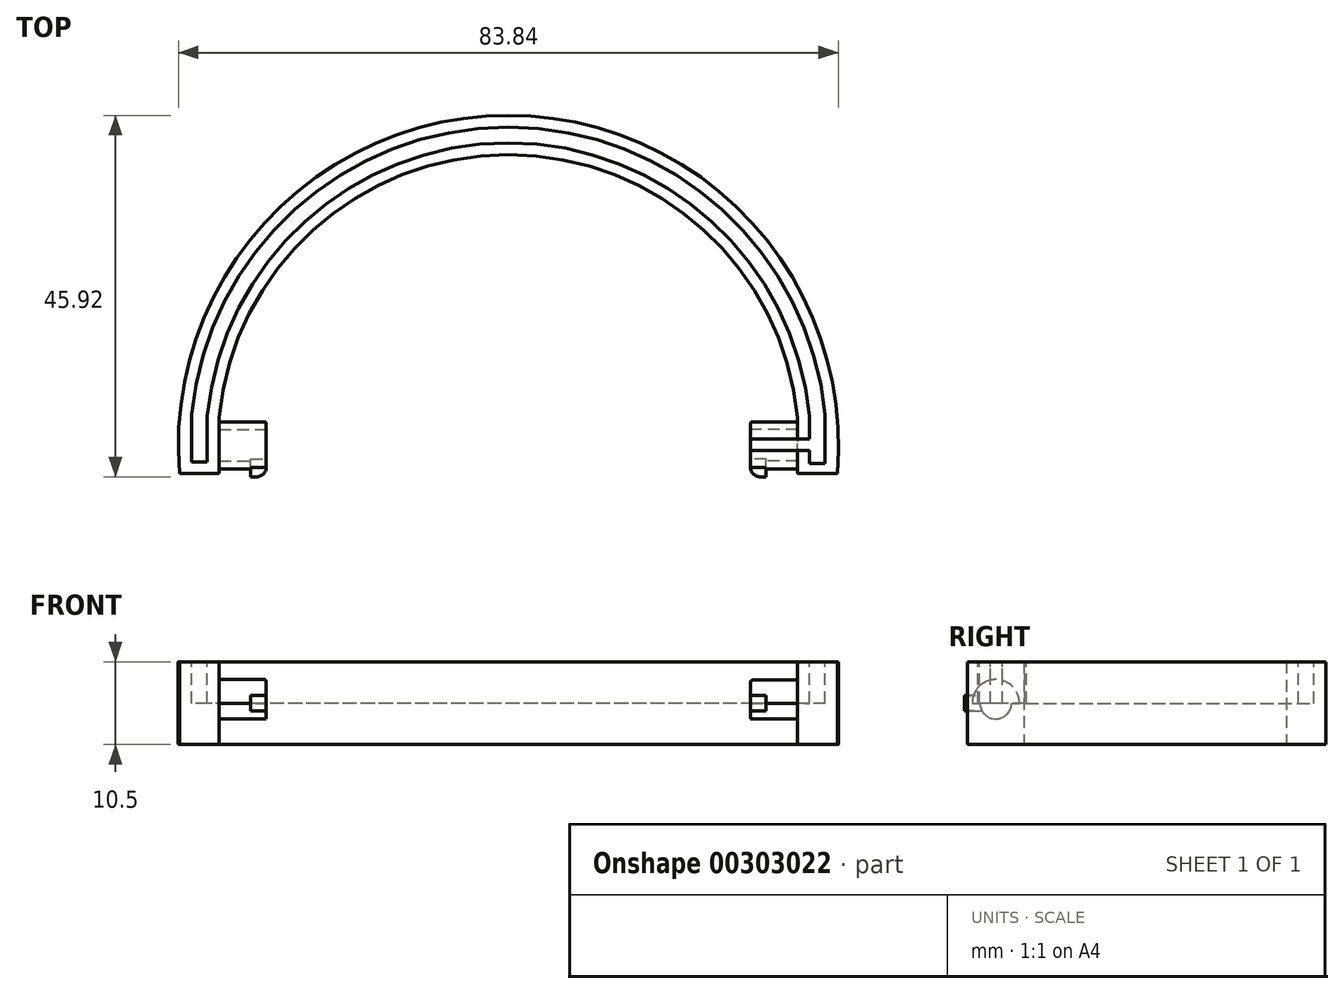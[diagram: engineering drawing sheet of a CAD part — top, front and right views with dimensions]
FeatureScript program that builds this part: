
annotation { "Feature Type Name" : "Feature", "Feature Type Description" : "" }
export const myFeature = defineFeature(function(context is Context, id is Id, definition is map)
    precondition{}
    {
        {
            var Q0;
            Q0=qCreatedBy(makeId("Top.planeOp"),FACE);
            var sketch = newSketch(context, id + "F0", { "sketchPlane" : qUnion([Q0])});
            skArc(sketch, "E0", {"start": v(36.75, 7.15) * mm, "mid": v(0, 40.5) * mm, "end": v(-36.75, 7.15) * mm});
            skPoint(sketch, "E1.center.orphan", {"position": v(0, 0) * mm});
            skArc(sketch, "E2.0", {"start": v(41.77, 0) * mm, "mid": v(0, 45.5) * mm, "end": v(-41.77, 0) * mm});
            skLineSegment(sketch, "E3", {"start": v(-36.75, 0) * mm, "end": v(-36.75, 7.15) * mm});
            skLineSegment(sketch, "E4", {"start": v(-36.75, 0) * mm, "end": v(-41.77, 0) * mm});
            skLineSegment(sketch, "E5", {"start": v(36.75, 0) * mm, "end": v(36.75, 7.15) * mm});
            skLineSegment(sketch, "E6", {"start": v(36.75, 0) * mm, "end": v(41.77, 0) * mm});
            skSolve(sketch);
        }
        {
            var Q0;
            Q0 = qSketchRegion(id + "F0", true);
            extrude(context, id + "F1", {"entities" : qUnion([Q0]), "depth" : 10.5 * mm});
        }
        {
            var Q0;
            Q0=makeQuery(id+"F1.opExtrude","SWEPT_FACE",FACE,{"disambiguationData":[OSD([sQuery(id+"F0.wireOp",EDGE,"E3")])]});
            var sketch = newSketch(context, id + "F2", { "sketchPlane" : qUnion([Q0])});
            skCircle(sketch, "E7", {"center": v(3.58, 5.25) * mm, "radius": 3 * mm});
            skPoint(sketch, "E7.centerSnap0", {"position": v(3.58, 0) * mm});
            skPoint(sketch, "E7.centerSnap1", {"position": v(0, 5.25) * mm});
            skSolve(sketch);
        }
        {
            var Q0;
            Q0=makeQuery(id+"F2.imprint","IMPRINT",FACE,{"disambiguationData":[TD([[makeQuery(id+"F2.imprint","IMPRINT",EDGE,{"derivedFrom":sQuery(id+"F2.wireOp",EDGE,"E7")}),1.0]])]});
            extrude(context, id + "F3", {"entities" : qUnion([Q0]), "operationType" : NewBodyOperationType.ADD, "depth" : 6 * mm});
        }
        {
            var Q0;
            Q0=makeQuery(id+"F1.opExtrude","SWEPT_FACE",FACE,{"disambiguationData":[OSD([sQuery(id+"F0.wireOp",EDGE,"E5")])]});
            var sketch = newSketch(context, id + "F4", { "sketchPlane" : qUnion([Q0])});
            skCircle(sketch, "E8", {"center": v(-3.58, 5.25) * mm, "radius": 3 * mm});
            skPoint(sketch, "E8.centerSnap0", {"position": v(-3.58, 10.5) * mm});
            skPoint(sketch, "E8.centerSnap1", {"position": v(0, 5.25) * mm});
            skSolve(sketch);
        }
        {
            var Q0;
            Q0 = qSketchRegion(id + "F4", true);
            extrude(context, id + "F5", {"entities" : qUnion([Q0]), "operationType" : NewBodyOperationType.ADD, "depth" : 6 * mm});
        }
        {
            var Q0;
            Q0=makeQuery(id+"F1.opExtrude","CAP_FACE",FACE,{"disambiguationData":[OSD([sQuery(id+"F0.wireOp",EDGE,"E0"),sQuery(id+"F0.wireOp",EDGE,"E2.0"),sQuery(id+"F0.wireOp",EDGE,"E3"),sQuery(id+"F0.wireOp",EDGE,"E4"),sQuery(id+"F0.wireOp",EDGE,"E5"),sQuery(id+"F0.wireOp",EDGE,"E6")])],"isStart":false});
            var sketch = newSketch(context, id + "F6", { "sketchPlane" : qUnion([Q0])});
            skArc(sketch, "E9.0", {"start": v(38.24, 7.3) * mm, "mid": v(0, 42) * mm, "end": v(-38.24, 7.3) * mm});
            skArc(sketch, "E10.0", {"start": v(40.23, 7.5) * mm, "mid": v(0, 44) * mm, "end": v(-40.23, 7.5) * mm});
            skLineSegment(sketch, "E11", {"start": v(-40.23, 7.5) * mm, "end": v(-40.23, 1.5) * mm});
            skLineSegment(sketch, "E12", {"start": v(-38.24, 7.3) * mm, "end": v(-38.24, 1.5) * mm});
            skLineSegment(sketch, "E13", {"start": v(-38.24, 1.5) * mm, "end": v(-40.23, 1.5) * mm});
            skLineSegment(sketch, "E14", {"start": v(38.24, 7.3) * mm, "end": v(38.24, 4.4) * mm});
            skLineSegment(sketch, "E15", {"start": v(40.23, 7.5) * mm, "end": v(40.23, 1.3) * mm});
            skLineSegment(sketch, "E16", {"start": v(40.23, 1.3) * mm, "end": v(38.24, 1.3) * mm});
            skLineSegment(sketch, "E17", {"start": v(30.74, 4.4) * mm, "end": v(38.24, 4.4) * mm});
            skLineSegment(sketch, "E18", {"start": v(30.74, 2.9) * mm, "end": v(38.24, 2.9) * mm});
            skPoint(sketch, "E19", {"position": v(38.24, 3.65) * mm});
            skLineSegment(sketch, "E20", {"start": v(30.74, 4.4) * mm, "end": v(30.74, 2.9) * mm});
            skLineSegment(sketch, "E21.trimOffspring", {"start": v(38.24, 2.9) * mm, "end": v(38.24, 1.3) * mm});
            skSolve(sketch);
        }
        {
            var Q0;
            Q0 = qSketchRegion(id + "F6", true);
            extrude(context, id + "F7", {"entities" : qUnion([Q0]), "operationType" : NewBodyOperationType.REMOVE, "oppositeDirection" : true, "depth" : 5.25 * mm});
        }
        {
            var Q0;
            Q0=makeQuery(id+"F5.opExtrude","CAP_FACE",FACE,{"disambiguationData":[OSD([sQuery(id+"F4.wireOp",EDGE,"E8")])],"isStart":false});
            var sketch = newSketch(context, id + "F8", { "sketchPlane" : qUnion([Q0])});
            skArc(sketch, "E22", {"start": v(-5.58, 5.25) * mm, "mid": v(-3.58, 3.25) * mm, "end": v(-1.58, 5.25) * mm});
            skLineSegment(sketch, "E23", {"start": v(-5.58, 5.25) * mm, "end": v(-6.58, 5.25) * mm});
            skLineSegment(sketch, "E24", {"start": v(-6.58, 5.25) * mm, "end": v(-5.58, 5.25) * mm});
            skLineSegment(sketch, "E25.trimOffspring", {"start": v(-1.58, 5.25) * mm, "end": v(-0.58, 5.25) * mm});
            skArc(sketch, "E26", {"start": v(-6.58, 5.25) * mm, "mid": v(-3.58, 2.25) * mm, "end": v(-0.58, 5.25) * mm});
            skSolve(sketch);
        }
        {
            var Q0;
            Q0=makeQuery(id+"F8.imprint","IMPRINT",FACE,{"disambiguationData":[TD([[makeQuery(id+"F8.imprint","IMPRINT",EDGE,{"derivedFrom":sQuery(id+"F8.wireOp",EDGE,"E22")}),-1.0]])]});
            extrude(context, id + "F9", {"entities" : qUnion([Q0]), "operationType" : NewBodyOperationType.REMOVE, "oppositeDirection" : true, "depth" : 6 * mm});
        }
        {
            var Q0;
            Q0=makeQuery(id+"F3.opExtrude","CAP_FACE",FACE,{"disambiguationData":[OSD([sQuery(id+"F2.wireOp",EDGE,"E7")])],"isStart":false});
            var sketch = newSketch(context, id + "F10", { "sketchPlane" : qUnion([Q0])});
            skArc(sketch, "E27", {"start": v(1.58, 5.25) * mm, "mid": v(3.58, 3.25) * mm, "end": v(5.58, 5.25) * mm});
            skLineSegment(sketch, "E28", {"start": v(5.58, 5.25) * mm, "end": v(6.58, 5.25) * mm});
            skLineSegment(sketch, "E29", {"start": v(6.58, 5.25) * mm, "end": v(5.58, 5.25) * mm});
            skLineSegment(sketch, "E30.trimOffspring", {"start": v(1.58, 5.25) * mm, "end": v(0.58, 5.25) * mm});
            skArc(sketch, "E31", {"start": v(0.58, 5.25) * mm, "mid": v(3.58, 2.25) * mm, "end": v(6.58, 5.25) * mm});
            skSolve(sketch);
        }
        {
            var Q0;
            Q0 = qSketchRegion(id + "F10", true);
            extrude(context, id + "F11", {"entities" : qUnion([Q0]), "operationType" : NewBodyOperationType.REMOVE, "oppositeDirection" : true, "depth" : 6 * mm});
        }
        {
            var Q0;
            Q0=makeQuery(id+"F5.opExtrude","CAP_FACE",FACE,{"disambiguationData":[OSD([sQuery(id+"F4.wireOp",EDGE,"E8")])],"isStart":false});
            var sketch = newSketch(context, id + "F12", { "sketchPlane" : qUnion([Q0])});
            skLineSegment(sketch, "E32.bottom", {"start": v(0.42, 6.25) * mm, "end": v(-1.58, 6.25) * mm});
            skLineSegment(sketch, "E32.top", {"start": v(0.42, 4.25) * mm, "end": v(-1.58, 4.25) * mm});
            skLineSegment(sketch, "E32.left", {"start": v(0.42, 6.25) * mm, "end": v(0.42, 4.25) * mm});
            skPoint(sketch, "E32.middle", {"position": v(-1.58, 5.25) * mm});
            skLineSegment(sketch, "E33", {"start": v(-1.58, 4.25) * mm, "end": v(-2.3, 4.25) * mm});
            skLineSegment(sketch, "E34", {"start": v(-2.3, 4.25) * mm, "end": v(-1.58, 6.25) * mm});
            skSolve(sketch);
        }
        {
            var Q0;
            Q0 = qSketchRegion(id + "F12", true);
            extrude(context, id + "F13", {"entities" : qUnion([Q0]), "operationType" : NewBodyOperationType.ADD, "oppositeDirection" : true, "depth" : 2 * mm});
        }
        {
            var Q0;
            Q0=makeQuery(id+"F3.opExtrude","CAP_FACE",FACE,{"disambiguationData":[OSD([sQuery(id+"F2.wireOp",EDGE,"E7")])],"isStart":false});
            var sketch = newSketch(context, id + "F14", { "sketchPlane" : qUnion([Q0])});
            skLineSegment(sketch, "E35.bottom", {"start": v(-0.42, 4.25) * mm, "end": v(1.58, 4.25) * mm});
            skLineSegment(sketch, "E35.top", {"start": v(-0.42, 6.25) * mm, "end": v(1.58, 6.25) * mm});
            skLineSegment(sketch, "E35.left", {"start": v(-0.42, 4.25) * mm, "end": v(-0.42, 6.25) * mm});
            skPoint(sketch, "E35.middle", {"position": v(1.58, 5.25) * mm});
            skLineSegment(sketch, "E36", {"start": v(1.58, 4.25) * mm, "end": v(2.92, 4.25) * mm});
            skLineSegment(sketch, "E37", {"start": v(2.92, 4.25) * mm, "end": v(1.58, 6.25) * mm});
            skSolve(sketch);
        }
        {
            var Q0;
            Q0 = qSketchRegion(id + "F14", true);
            extrude(context, id + "F15", {"entities" : qUnion([Q0]), "operationType" : NewBodyOperationType.ADD, "oppositeDirection" : true, "depth" : 2 * mm});
        }
        {
            var Q0;
            Q0=makeQuery(id+"F15.opExtrude","CAP_EDGE",EDGE,{"disambiguationData":[OSD([sQuery(id+"F14.wireOp",EDGE,"E35.left")])],"isStart":true});
            var Q1;
            Q1=makeQuery(id+"F13.opExtrude","CAP_EDGE",EDGE,{"disambiguationData":[OSD([sQuery(id+"F12.wireOp",EDGE,"E32.left")])],"isStart":true});
            fillet(context, id + "F16", {"entities" : qUnion([Q0, Q1]), "radius" : 1.25 * mm, "tangentPropagation" : true, "allowEdgeOverflow" : false});
        }
        {
            var Q0;
            {var subQ0=sQuery(id+"F4.wireOp",EDGE,"E8");Q0=makeQuery(id+"F9.boolean.opBoolean","SPLIT",EDGE,{"disambiguationData":[TD([makeQuery(id+"F7.boolean.opBoolean","COPY",FACE,{"derivedFrom":makeQuery(id+"F7.opExtrude","SWEPT_FACE",FACE,{"disambiguationData":[OSD([sQuery(id+"F6.wireOp",EDGE,"E17")])]})})])],"derivedFrom":makeQuery(id+"F5.opExtrude","CAP_EDGE",EDGE,{"disambiguationData":[OSD([subQ0])],"isStart":false})});}
            var Q1;
            {var subQ0=sQuery(id+"F4.wireOp",EDGE,"E8");Q1=makeQuery(id+"F9.boolean.opBoolean","SPLIT",EDGE,{"disambiguationData":[TD([makeQuery(id+"F7.boolean.opBoolean","COPY",FACE,{"derivedFrom":makeQuery(id+"F7.opExtrude","SWEPT_FACE",FACE,{"disambiguationData":[OSD([sQuery(id+"F6.wireOp",EDGE,"E18")])]})})])],"derivedFrom":makeQuery(id+"F5.opExtrude","CAP_EDGE",EDGE,{"disambiguationData":[OSD([subQ0])],"isStart":false})});}
            var Q2;
            Q2=makeQuery(id+"F9.boolean.opBoolean","COPY",EDGE,{"derivedFrom":makeQuery(id+"F9.opExtrude","CAP_EDGE",EDGE,{"disambiguationData":[OSD([sQuery(id+"F8.wireOp",EDGE,"E22")])],"isStart":true})});
            var Q3;
            Q3=makeQuery(id+"F3.opExtrude","CAP_EDGE",EDGE,{"disambiguationData":[OSD([sQuery(id+"F2.wireOp",EDGE,"E7")])],"isStart":false});
            var Q4;
            Q4=makeQuery(id+"F11.boolean.opBoolean","COPY",EDGE,{"derivedFrom":makeQuery(id+"F11.opExtrude","CAP_EDGE",EDGE,{"disambiguationData":[OSD([sQuery(id+"F10.wireOp",EDGE,"E27")])],"isStart":true})});
            fillet(context, id + "F17", {"entities" : qUnion([Q0, Q1, Q2, Q3, Q4]), "radius" : .25 * mm, "tangentPropagation" : true, "allowEdgeOverflow" : false});
        }
    });
